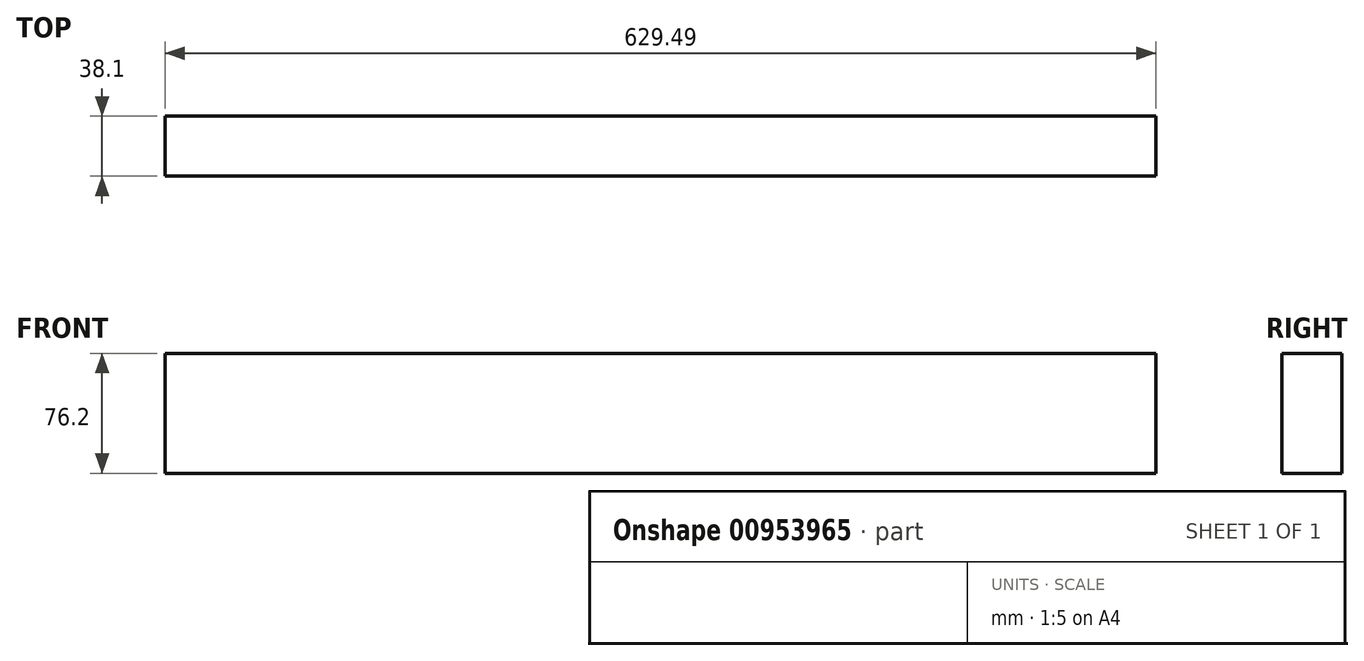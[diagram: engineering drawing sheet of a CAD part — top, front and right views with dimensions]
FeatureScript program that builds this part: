
annotation { "Feature Type Name" : "Feature", "Feature Type Description" : "" }
export const myFeature = defineFeature(function(context is Context, id is Id, definition is map)
    precondition{}
    {
        {
            var Q0;
            Q0=qCreatedBy(makeId("Front.planeOp"),FACE);
            var sketch = newSketch(context, id + "F0", { "sketchPlane" : qUnion([Q0])});
            skLineSegment(sketch, "E0.bottom", {"start": v(0, 0) * mm, "end": v(629.49, 0) * mm});
            skLineSegment(sketch, "E0.top", {"start": v(0, 76.2) * mm, "end": v(629.49, 76.2) * mm});
            skLineSegment(sketch, "E0.left", {"start": v(0, 0) * mm, "end": v(0, 76.2) * mm});
            skLineSegment(sketch, "E0.right", {"start": v(629.49, 0) * mm, "end": v(629.49, 76.2) * mm});
            skSolve(sketch);
        }
        {
            var Q0;
            Q0 = qSketchRegion(id + "F0", true);
            extrude(context, id + "F1", {"entities" : qUnion([Q0]), "depth" : 38.1 * mm, "offsetDistance" : 25.4 * mm});
        }
    });
